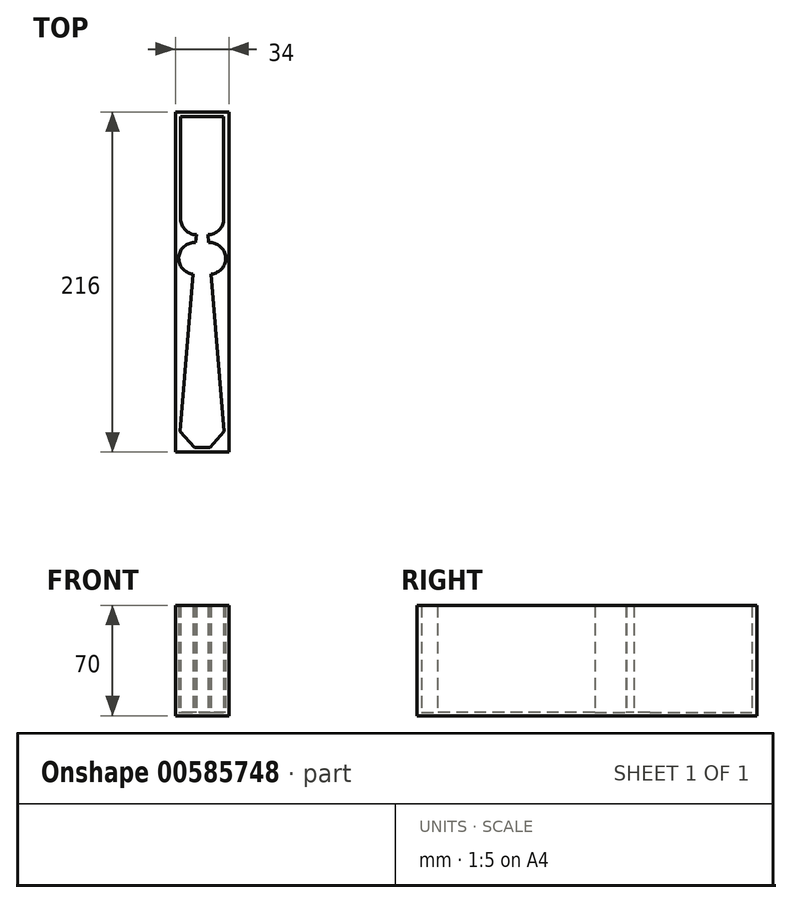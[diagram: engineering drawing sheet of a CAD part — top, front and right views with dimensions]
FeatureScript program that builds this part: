
annotation { "Feature Type Name" : "Feature", "Feature Type Description" : "" }
export const myFeature = defineFeature(function(context is Context, id is Id, definition is map)
    precondition{}
    {
        {
            var Q0;
            Q0=qCreatedBy(makeId("Top.planeOp"),FACE);
            var sketch = newSketch(context, id + "F0", { "sketchPlane" : qUnion([Q0])});
            skLineSegment(sketch, "E0.bottom", {"start": v(9, 0) * mm, "end": v(14, 0) * mm});
            skLineSegment(sketch, "E0.top", {"start": v(0.35, 210) * mm, "end": v(14, 210) * mm});
            skLineSegment(sketch, "E1", {"start": v(9, 0) * mm, "end": v(0, 10) * mm});
            skPoint(sketch, "E2.orphan", {"position": v(14, 0) * mm});
            skArc(sketch, "E3", {"start": v(10.32, 135) * mm, "mid": v(3.27, 137.94) * mm, "end": v(0.35, 145) * mm});
            skPoint(sketch, "E4.orphan", {"position": v(14, 210) * mm});
            skLineSegment(sketch, "E5.0", {"start": v(-3, -3) * mm, "end": v(14, -3) * mm});
            skLineSegment(sketch, "E5.1", {"start": v(-3, 213) * mm, "end": v(14, 213) * mm});
            skLineSegment(sketch, "E5.3", {"start": v(-3, -3) * mm, "end": v(-3, 213) * mm});
            skPoint(sketch, "E6.orphan", {"position": v(0, 0) * mm});
            skLineSegment(sketch, "E7.trimOffspring", {"start": v(0.35, 145) * mm, "end": v(0.35, 210) * mm});
            skLineSegment(sketch, "E8", {"start": v(10.32, 135) * mm, "end": v(9.9, 129.97) * mm});
            skArc(sketch, "E9", {"start": v(9.9, 129.97) * mm, "mid": v(-0.88, 120.82) * mm, "end": v(8.26, 110.03) * mm});
            skLineSegment(sketch, "E10.trimOffspring", {"start": v(8.26, 110.03) * mm, "end": v(0, 10) * mm});
            skLineSegment(sketch, "E11.MirrorCS", {"start": v(19, 0) * mm, "end": v(14, 0) * mm});
            skLineSegment(sketch, "E12.MirrorCS", {"start": v(31, -3) * mm, "end": v(14, -3) * mm});
            skLineSegment(sketch, "E13.MirrorCS", {"start": v(17.68, 135) * mm, "end": v(18.1, 129.97) * mm});
            skLineSegment(sketch, "E14.MirrorCS", {"start": v(31, 213) * mm, "end": v(14, 213) * mm});
            skArc(sketch, "E15.MirrorCS", {"start": v(17.68, 135) * mm, "mid": v(24.73, 137.94) * mm, "end": v(27.65, 145) * mm});
            skLineSegment(sketch, "E16.MirrorCS", {"start": v(19, 0) * mm, "end": v(28, 10) * mm});
            skLineSegment(sketch, "E17.MirrorCS", {"start": v(27.65, 210) * mm, "end": v(14, 210) * mm});
            skLineSegment(sketch, "E18.MirrorCS", {"start": v(19.74, 110.03) * mm, "end": v(28, 10) * mm});
            skLineSegment(sketch, "E19.MirrorCS", {"start": v(31, -3) * mm, "end": v(31, 213) * mm});
            skPoint(sketch, "E20.MirrorP", {"position": v(28, 0) * mm});
            skLineSegment(sketch, "E21.MirrorCS", {"start": v(27.65, 145) * mm, "end": v(27.65, 210) * mm});
            skArc(sketch, "E22.MirrorCS", {"start": v(18.1, 129.97) * mm, "mid": v(28.88, 120.82) * mm, "end": v(19.74, 110.03) * mm});
            skSolve(sketch);
        }
        {
            var Q0;
            {var subQ6=sQuery(id+"F0.wireOp",EDGE,"E0.top");Q0=makeQuery(id+"F0.imprint","IMPRINT",FACE,{"disambiguationData":[TD([[makeQuery(id+"F0.imprint","IMPRINT",EDGE,{"derivedFrom":subQ6}),1.0]])]});}
            extrude(context, id + "F1", {"entities" : qUnion([Q0]), "depth" : 68 * mm, "offsetDistance" : 25 * mm});
        }
        {
            var Q0;
            Q0=makeQuery(id+"F0.imprint","IMPRINT",FACE,{"disambiguationData":[TD([[makeQuery(id+"F0.imprint","IMPRINT",EDGE,{"derivedFrom":sQuery(id+"F0.wireOp",EDGE,"E0.bottom")}),-1.0]])]});
            var Q1;
            Q1=makeQuery(id+"F0.imprint","IMPRINT",FACE,{"disambiguationData":[TD([[makeQuery(id+"F0.imprint","IMPRINT",EDGE,{"derivedFrom":sQuery(id+"F0.wireOp",EDGE,"E0.bottom")}),1.0]])]});
            extrude(context, id + "F2", {"entities" : qUnion([Q0, Q1]), "operationType" : NewBodyOperationType.ADD, "oppositeDirection" : true, "depth" : 2 * mm, "offsetDistance" : 25 * mm});
        }
    });
